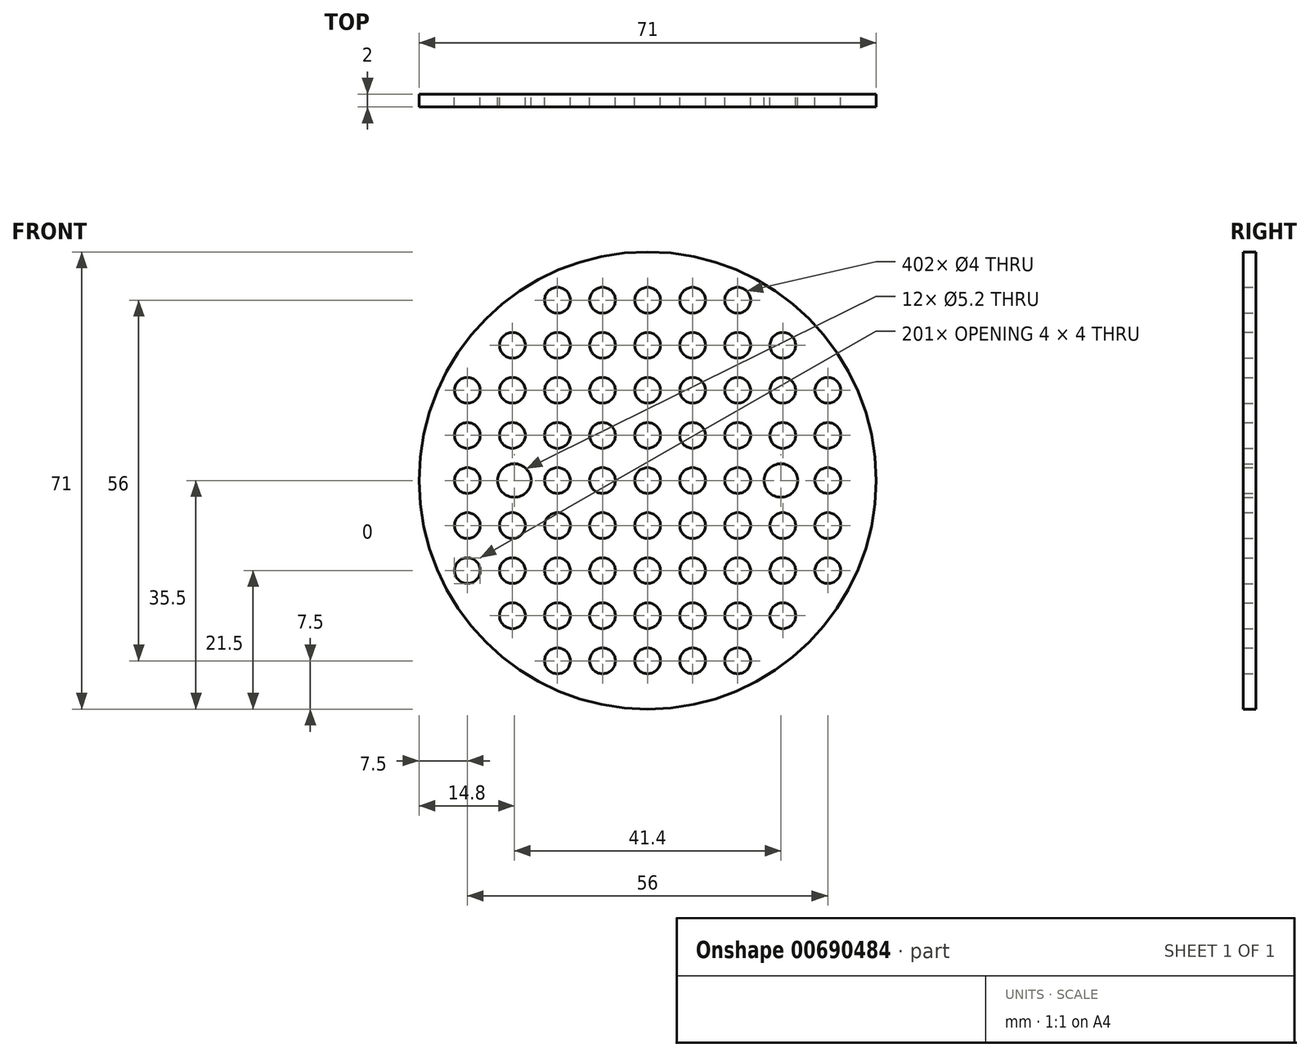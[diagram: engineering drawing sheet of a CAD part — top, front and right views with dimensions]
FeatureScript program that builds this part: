
annotation { "Feature Type Name" : "Feature", "Feature Type Description" : "" }
export const myFeature = defineFeature(function(context is Context, id is Id, definition is map)
    precondition{}
    {
        {
            var Q0;
            Q0=qCreatedBy(makeId("Front.planeOp"),FACE);
            var sketch = newSketch(context, id + "F0", { "sketchPlane" : qUnion([Q0])});
            skPoint(sketch, "E0.orphan", {"position": v(0, 118.02) * mm});
            skPoint(sketch, "E1.start.orphan", {"position": v(0, 0) * mm});
            skPoint(sketch, "E2.start.orphan", {"position": v(0, 59.01) * mm});
            skCircle(sketch, "E3", {"center": v(0, 0) * mm, "radius": 35.5 * mm});
            skLineSegment(sketch, "E4", {"start": v(35.5, 0) * mm, "end": v(23.3, 0) * mm});
            skLineSegment(sketch, "E5", {"start": v(-35.5, 0) * mm, "end": v(-23.3, 0) * mm});
            skCircle(sketch, "E6", {"center": v(20.7, 0) * mm, "radius": 2.6 * mm});
            skCircle(sketch, "E7", {"center": v(-20.7, 0) * mm, "radius": 2.6 * mm});
            skSolve(sketch);
        }
        {
            var Q0;
            Q0 = qSketchRegion(id + "F0", true);
            extrude(context, id + "F1", {"entities" : qUnion([Q0]), "depth" : 2 * mm, "offsetDistance" : 25 * mm});
        }
        {
            var Q0;
            Q0=makeQuery(id+"F1.opExtrude","CAP_FACE",FACE,{"disambiguationData":[OSD([sQuery(id+"F0.wireOp",EDGE,"E3"),sQuery(id+"F0.wireOp",EDGE,"E6"),sQuery(id+"F0.wireOp",EDGE,"E7")])],"isStart":true});
            var sketch = newSketch(context, id + "F2", { "sketchPlane" : qUnion([Q0])});
            skCircle(sketch, "E8", {"center": v(0, 0) * mm, "radius": 2 * mm});
            skCircle(sketch, "E9.0.1.0", {"center": v(0, 7) * mm, "radius": 2 * mm});
            skCircle(sketch, "E9.0.2.0", {"center": v(0, 14) * mm, "radius": 2 * mm});
            skCircle(sketch, "E9.0.3.0", {"center": v(0, 21) * mm, "radius": 2 * mm});
            skCircle(sketch, "E9.0.4.0", {"center": v(0, 28) * mm, "radius": 2 * mm});
            skCircle(sketch, "E9.1.0.0", {"center": v(7, 0) * mm, "radius": 2 * mm});
            skCircle(sketch, "E9.1.1.0", {"center": v(7, 7) * mm, "radius": 2 * mm});
            skCircle(sketch, "E9.1.2.0", {"center": v(7, 14) * mm, "radius": 2 * mm});
            skCircle(sketch, "E9.1.3.0", {"center": v(7, 21) * mm, "radius": 2 * mm});
            skCircle(sketch, "E9.1.4.0", {"center": v(7, 28) * mm, "radius": 2 * mm});
            skCircle(sketch, "E9.2.0.0", {"center": v(14, 0) * mm, "radius": 2 * mm});
            skCircle(sketch, "E9.2.1.0", {"center": v(14, 7) * mm, "radius": 2 * mm});
            skCircle(sketch, "E9.2.2.0", {"center": v(14, 14) * mm, "radius": 2 * mm});
            skCircle(sketch, "E9.2.3.0", {"center": v(14, 21) * mm, "radius": 2 * mm});
            skCircle(sketch, "E9.2.4.0", {"center": v(14, 28) * mm, "radius": 2 * mm});
            skCircle(sketch, "E9.3.1.0", {"center": v(21, 7) * mm, "radius": 2 * mm});
            skCircle(sketch, "E9.3.2.0", {"center": v(21, 14) * mm, "radius": 2 * mm});
            skCircle(sketch, "E9.3.3.0", {"center": v(21, 21) * mm, "radius": 2 * mm});
            skCircle(sketch, "E9.4.0.0", {"center": v(28, 0) * mm, "radius": 2 * mm});
            skCircle(sketch, "E9.4.1.0", {"center": v(28, 7) * mm, "radius": 2 * mm});
            skCircle(sketch, "E9.4.2.0", {"center": v(28, 14) * mm, "radius": 2 * mm});
            skLineSegment(sketch, "E9.direction1", {"start": v(0, 0) * mm, "end": v(7, 0) * mm, "construction": true});
            skLineSegment(sketch, "E9.direction2", {"start": v(0, 0) * mm, "end": v(0, 7) * mm, "construction": true});
            skCircle(sketch, "E10.1.0.0", {"center": v(-7, 28) * mm, "radius": 2 * mm});
            skCircle(sketch, "E10.1.0.1", {"center": v(-7, 21) * mm, "radius": 2 * mm});
            skCircle(sketch, "E10.1.0.2", {"center": v(-7, 14) * mm, "radius": 2 * mm});
            skCircle(sketch, "E10.1.0.4", {"center": v(-7, 7) * mm, "radius": 2 * mm});
            skCircle(sketch, "E10.1.0.5", {"center": v(-7, 0) * mm, "radius": 2 * mm});
            skCircle(sketch, "E10.2.0.0", {"center": v(-14, 28) * mm, "radius": 2 * mm});
            skCircle(sketch, "E10.2.0.1", {"center": v(-14, 21) * mm, "radius": 2 * mm});
            skCircle(sketch, "E10.2.0.2", {"center": v(-14, 14) * mm, "radius": 2 * mm});
            skCircle(sketch, "E10.2.0.4", {"center": v(-14, 7) * mm, "radius": 2 * mm});
            skCircle(sketch, "E10.2.0.5", {"center": v(-14, 0) * mm, "radius": 2 * mm});
            skCircle(sketch, "E10.3.0.1", {"center": v(-21, 21) * mm, "radius": 2 * mm});
            skCircle(sketch, "E10.3.0.2", {"center": v(-21, 14) * mm, "radius": 2 * mm});
            skCircle(sketch, "E10.3.0.4", {"center": v(-21, 7) * mm, "radius": 2 * mm});
            skCircle(sketch, "E10.4.0.2", {"center": v(-28, 14) * mm, "radius": 2 * mm});
            skCircle(sketch, "E10.4.0.4", {"center": v(-28, 7) * mm, "radius": 2 * mm});
            skCircle(sketch, "E10.4.0.5", {"center": v(-28, 0) * mm, "radius": 2 * mm});
            skLineSegment(sketch, "E10.direction1", {"start": v(0, 28) * mm, "end": v(-7, 28) * mm, "construction": true});
            skCircle(sketch, "E11.0.1.0", {"center": v(-28, -7) * mm, "radius": 2 * mm});
            skCircle(sketch, "E11.0.1.2", {"center": v(-21, -7) * mm, "radius": 2 * mm});
            skCircle(sketch, "E11.0.1.3", {"center": v(-14, -7) * mm, "radius": 2 * mm});
            skCircle(sketch, "E11.0.1.5", {"center": v(28, -7) * mm, "radius": 2 * mm});
            skCircle(sketch, "E11.0.1.6", {"center": v(21, -7) * mm, "radius": 2 * mm});
            skCircle(sketch, "E11.0.1.7", {"center": v(14, -7) * mm, "radius": 2 * mm});
            skCircle(sketch, "E11.0.1.8", {"center": v(7, -7) * mm, "radius": 2 * mm});
            skCircle(sketch, "E11.0.1.9", {"center": v(0, -7) * mm, "radius": 2 * mm});
            skCircle(sketch, "E11.0.1.10", {"center": v(-7, -7) * mm, "radius": 2 * mm});
            skCircle(sketch, "E11.0.2.0", {"center": v(-28, -14) * mm, "radius": 2 * mm});
            skCircle(sketch, "E11.0.2.2", {"center": v(-21, -14) * mm, "radius": 2 * mm});
            skCircle(sketch, "E11.0.2.3", {"center": v(-14, -14) * mm, "radius": 2 * mm});
            skCircle(sketch, "E11.0.2.5", {"center": v(28, -14) * mm, "radius": 2 * mm});
            skCircle(sketch, "E11.0.2.6", {"center": v(21, -14) * mm, "radius": 2 * mm});
            skCircle(sketch, "E11.0.2.7", {"center": v(14, -14) * mm, "radius": 2 * mm});
            skCircle(sketch, "E11.0.2.8", {"center": v(7, -14) * mm, "radius": 2 * mm});
            skCircle(sketch, "E11.0.2.9", {"center": v(0, -14) * mm, "radius": 2 * mm});
            skCircle(sketch, "E11.0.2.10", {"center": v(-7, -14) * mm, "radius": 2 * mm});
            skCircle(sketch, "E11.0.3.2", {"center": v(-21, -21) * mm, "radius": 2 * mm});
            skCircle(sketch, "E11.0.3.3", {"center": v(-14, -21) * mm, "radius": 2 * mm});
            skCircle(sketch, "E11.0.3.6", {"center": v(21, -21) * mm, "radius": 2 * mm});
            skCircle(sketch, "E11.0.3.7", {"center": v(14, -21) * mm, "radius": 2 * mm});
            skCircle(sketch, "E11.0.3.8", {"center": v(7, -21) * mm, "radius": 2 * mm});
            skCircle(sketch, "E11.0.3.9", {"center": v(0, -21) * mm, "radius": 2 * mm});
            skCircle(sketch, "E11.0.3.10", {"center": v(-7, -21) * mm, "radius": 2 * mm});
            skCircle(sketch, "E11.0.4.3", {"center": v(-14, -28) * mm, "radius": 2 * mm});
            skCircle(sketch, "E11.0.4.7", {"center": v(14, -28) * mm, "radius": 2 * mm});
            skCircle(sketch, "E11.0.4.8", {"center": v(7, -28) * mm, "radius": 2 * mm});
            skCircle(sketch, "E11.0.4.9", {"center": v(0, -28) * mm, "radius": 2 * mm});
            skCircle(sketch, "E11.0.4.10", {"center": v(-7, -28) * mm, "radius": 2 * mm});
            skLineSegment(sketch, "E11.direction1", {"start": v(-28, 0) * mm, "end": v(-53, 0) * mm, "construction": true});
            skLineSegment(sketch, "E11.direction2", {"start": v(-28, 0) * mm, "end": v(-28, -7) * mm, "construction": true});
            skSolve(sketch);
        }
        {
            var Q0;
            Q0 = qSketchRegion(id + "F2", true);
            extrude(context, id + "F3", {"entities" : qUnion([Q0]), "operationType" : NewBodyOperationType.REMOVE, "oppositeDirection" : true, "depth" : 25 * mm, "offsetDistance" : 25 * mm});
        }
    });
